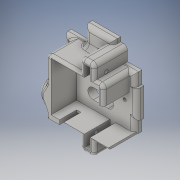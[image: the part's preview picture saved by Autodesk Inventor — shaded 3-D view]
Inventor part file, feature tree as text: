
AUTODESK INVENTOR PART (.ipt)
format: ipt  version: 2016 (Build 200138000, 138)  size: 679,424 bytes
history: native  units: in
note: dims shown in document units (in); Inventor stores cm internally (conversion verified against a paired STEP export)
features: sketch x16, extrude x12, fillet x6, hole x2, plane x2
ambient origin geometry x8: Origin, YZ Plane, XZ Plane, XY Plane, X Axis, Y Axis, Z Axis, Center Point
bodies: Solid1 (feature_tree)
feature tree (38):
  extrude  "Extrusion1"  Depth=0.1378in
  extrude  "Extrusion4"  Depth=0.9016in
  extrude  "Extrusion5"  Depth=0.1063in
  hole  "Hole3"  [1 undecoded]
  plane  "Work Plane5"
  extrude  "Extrusion6"  Depth=0.1654in
  plane  "Work Plane6"
  sketch  "Sketch21"  dims[d91=0.2992in d92=0.2165in d93=0.2165in d95=0.9016in d97=0.0787in]
  extrude  "Extrusion7"  Depth=0.2165in
  fillet  "Fillet13"  Radius=0.2165in
  fillet  "Fillet14"  Radius=0.9016in
  fillet  "Fillet16"  Radius=0.0787in
  sketch  "Sketch23"  dims[d100=0.0787in d101=0.0787in]
  extrude  "Extrusion8"  Depth=0.0787in
  extrude  "Extrusion9"  Depth=0.0787in
  sketch  "Sketch26"  dims[d107=0.0394in d108=0.0394in]
  sketch  "Sketch27"  dims[d109=0.0394in d110=0.1575in]
  extrude  "Extrusion10"  Depth=0.1693in
  extrude  "Extrusion11"  Depth=0.0394in
  sketch  "Sketch28"  dims[d111=0.0787in d112=0.0787in d113=0.0394in d114=0.9016in d125=0.0984in]
  extrude  "Extrusion12"  Depth=0.0394in
  extrude  "Extrusion13"  Depth=0.1575in
  extrude  "Extrusion14"  Depth=0.0787in
  fillet  "Fillet17"  Radius=0.0394in
  fillet  "Fillet18"  Radius=0.9016in
  fillet  "Fillet19"  Radius=0.0984in
  hole  "Hole4"  [1 undecoded]
  sketch  "Sketch1"  dims[d2=0.1378in d3=0.0in d6=0.8976in d9=0.357in d10=0.7139in]
  sketch  "Sketch12"  dims[d11=0.0787in d12=0.0787in d13=0.0787in d14=0.0787in d82=0.9016in d83=0.8858in]
  sketch  "Sketch14"  dims[d85=0.1063in d86=0.1063in]
  sketch  "Sketch17"  dims[d87=0.6142in d88=0.6142in]
  sketch  "Sketch18"  dims[d89=0.1654in d90=0.1654in]
  sketch  "Sketch22"  dims[d98=0.0787in d99=0.0787in]
  sketch  "Sketch24"  dims[d102=0.0787in d103=0.1693in]
  sketch  "Sketch25"  dims[d105=0.0787in d106=0.0394in]
  sketch  "Sketch29"  dims[d130=0.185in d132=0.3543in]
  sketch  "Sketch30"  dims[d133=0.2165in]
  sketch  "Sketch31"  dims[d134=0.4724in d135=0.0in d136=0.0787in d137=0.315in d138=0.0in d139=0.0787in d144=0.0394in d145=0.7461in d146=0.0394in d147=0.07in d148=0.2362in d149=0.119in d150=0.0787in d151=0.5635in d152=0.315in d153=0.8108in d156=0.2717in d157=0.2323in d158=0.2835in d159=0.4016in d160=0.1575in d161=0.0in d164=0.2559in d165=0.0394in d166=0.1575in d167=0.0in d169=0.1535in d170=0.0787in d172=0.0394in d173=0.1969in d174=0.1969in d178=0.1575in d179=0.1575in d182=0.2756in d183=0.2756in d184=0.2067in d185=0.2067in d186=0.2067in d187=0.3937in d188=0.0in d189=0.2559in d190=0.3937in d191=0.0in d192=0.5197in d193=0.3896in d194=0.3896in d195=0.5197in d196=0.3896in d197=0.3896in d198=0.0807in d199=0.0in d200=0.0807in d201=0.0in d202=0.5197in d203=0.4862in d204=0.4862in d205=0.5197in d206=0.4862in d207=0.4862in d208=0.0394in d209=0.0in d210=0.0394in d211=0.0in d212=0.1969in d213=0.0in d214=0.0in d215=0.0591in d216=0.0787in d217=0.0787in d218=0.0in d219=0.2756in d220=0.2598in d221=0.2165in d222=0.2598in d223=0.2756in d224=0.2625in d225=0.0591in d226=0.2362in d227=0.1575in d228=0.0787in d229=90.0deg d230=0.315in d231=0.8108in d232=0.1969in d233=0.2598in d234=0.2598in d235=0.2598in d26=0.0394in d27=0.0394in]
note: 2 required parameter values undecoded (feature->parameter linkage not recoverable at this tier; creation-order binding heuristic only, values carry confidence <= 0.55)
